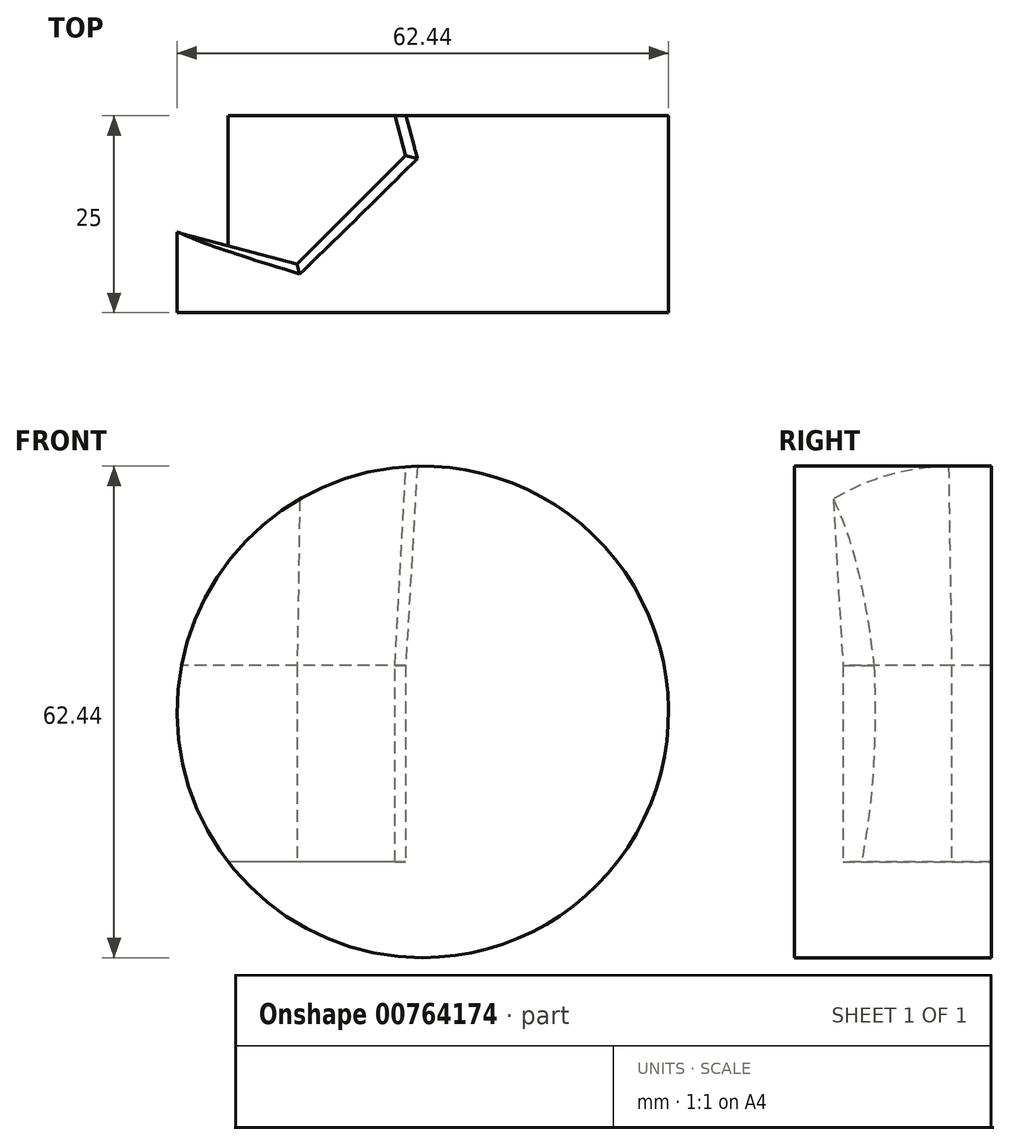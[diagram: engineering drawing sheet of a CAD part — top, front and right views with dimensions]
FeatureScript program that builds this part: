
annotation { "Feature Type Name" : "Feature", "Feature Type Description" : "" }
export const myFeature = defineFeature(function(context is Context, id is Id, definition is map)
    precondition{}
    {
        {
            var Q0;
            Q0=qCreatedBy(makeId("Front.planeOp"),FACE);
            var sketch = newSketch(context, id + "F0", { "sketchPlane" : qUnion([Q0])});
            skCircle(sketch, "E0", {"center": v(23.86, -5.93) * mm, "radius": 31.22 * mm});
            skSolve(sketch);
        }
        {
            var Q0;
            Q0 = qSketchRegion(id + "F0", true);
            extrude(context, id + "F1", {"entities" : qUnion([Q0]), "depth" : 25 * mm, "offsetDistance" : 25 * mm});
        }
        {
            var Q0;
            Q0=qCreatedBy(makeId("Top.planeOp"),FACE);
            var sketch = newSketch(context, id + "F2", { "sketchPlane" : qUnion([Q0])});
            skCircle(sketch, "E1.cCircle", {"center": v(2.84, 0) * mm, "radius": 16.9 * mm, "construction": true});
            skLineSegment(sketch, "E1.0", {"start": v(16.62, 13.81) * mm, "end": v(21.7, -5.03) * mm});
            skLineSegment(sketch, "E1.1", {"start": v(21.7, -5.03) * mm, "end": v(7.9, -18.85) * mm});
            skLineSegment(sketch, "E1.2", {"start": v(7.9, -18.85) * mm, "end": v(-10.95, -13.81) * mm});
            skLineSegment(sketch, "E1.3", {"start": v(-10.95, -13.81) * mm, "end": v(-16.02, 5.03) * mm});
            skLineSegment(sketch, "E1.4", {"start": v(-16.02, 5.03) * mm, "end": v(-2.23, 18.85) * mm});
            skLineSegment(sketch, "E1.5", {"start": v(-2.23, 18.85) * mm, "end": v(16.62, 13.81) * mm});
            skPoint(sketch, "E1.0.midPoint", {"position": v(19.16, 4.39) * mm});
            skSolve(sketch);
        }
        {
            var Q0;
            Q0 = qSketchRegion(id + "F2", true);
            extrude(context, id + "F3", {"entities" : qUnion([Q0]), "depth" : 44 * mm, "offsetDistance" : 25 * mm, "hasDraft" : true, "draftAngle" : 3 * degree, "hasSecondDirection" : true, "secondDirectionOppositeDirection" : true, "secondDirectionDepth" : 25 * mm});
        }
        {
            var Q0;
            Q0=makeQuery(id+"F3.*.split.splitOp","SPLIT",BODY,{"derivedFrom":makeQuery(id+"F3.opExtrude","SWEPT_BODY",BODY,{"disambiguationData":[OSD([sQuery(id+"F2.wireOp",EDGE,"E1.0"),sQuery(id+"F2.wireOp",EDGE,"E1.1"),sQuery(id+"F2.wireOp",EDGE,"E1.2"),sQuery(id+"F2.wireOp",EDGE,"E1.3"),sQuery(id+"F2.wireOp",EDGE,"E1.4"),sQuery(id+"F2.wireOp",EDGE,"E1.5")])]})});
            var Q1;
            Q1=makeQuery(id+"F1.opExtrude","SWEPT_BODY",BODY,{"disambiguationData":[OSD([sQuery(id+"F0.wireOp",EDGE,"E0")])]});
            booleanBodies(context, id + "F4", {"operationType" : BooleanOperationType.SUBTRACTION, "tools" : qUnion([Q0]), "targets" : qUnion([Q1])});
        }
    });
